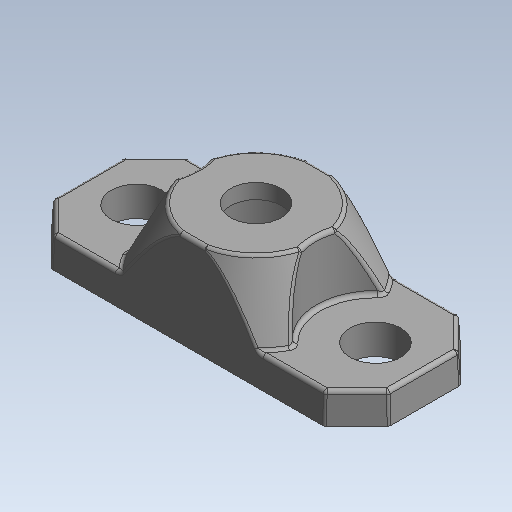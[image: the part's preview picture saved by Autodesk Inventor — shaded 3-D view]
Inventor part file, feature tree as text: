
AUTODESK INVENTOR PART (.ipt)
format: ipt  version: 2020 (Build 240168000, 168)  size: 369,664 bytes
history: native  units: mm (DEFAULTED — no unit token found)
features: fillet x1
ambient origin geometry x8: Origin, YZ Plane, XZ Plane, XY Plane, X Axis, Y Axis, Z Axis, Center Point
bodies: Solid1 (feature_tree)
feature tree (1):
  fillet  "Fillet6"  [1 undecoded]
note: 1 required parameter value undecoded (feature->parameter linkage not recoverable at this tier; creation-order binding heuristic only, values carry confidence <= 0.55)
